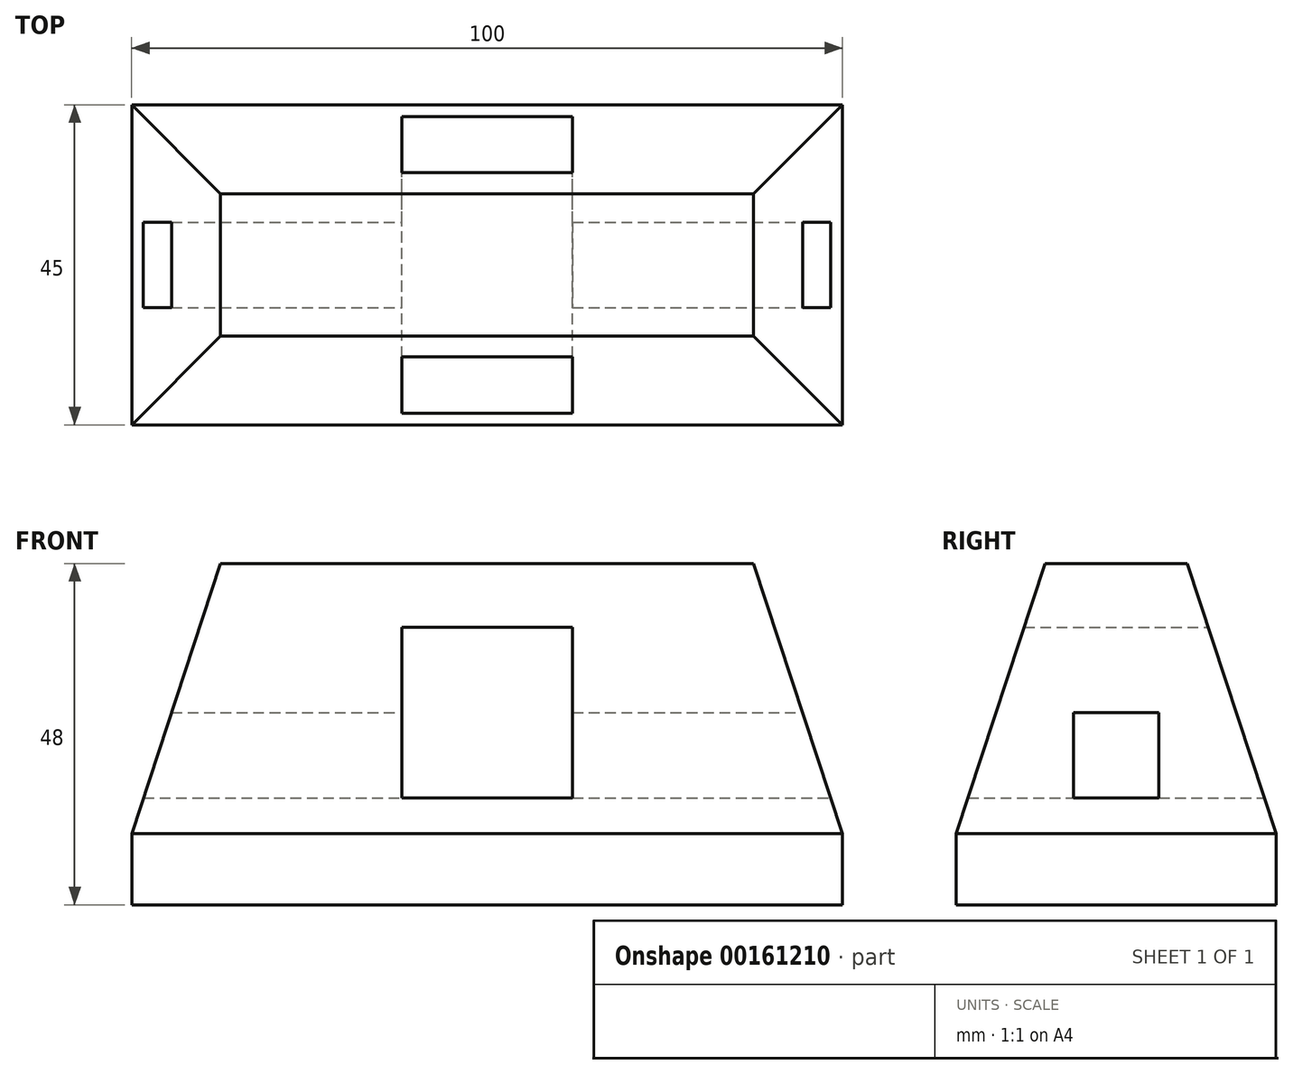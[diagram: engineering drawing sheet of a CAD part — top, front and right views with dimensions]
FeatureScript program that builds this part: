
annotation { "Feature Type Name" : "Feature", "Feature Type Description" : "" }
export const myFeature = defineFeature(function(context is Context, id is Id, definition is map)
    precondition{}
    {
        {
            var Q0;
            Q0=qCreatedBy(makeId("Top.planeOp"),FACE);
            var sketch = newSketch(context, id + "F0", { "sketchPlane" : qUnion([Q0])});
            skLineSegment(sketch, "E0.bottom", {"start": v(-62.77, 15.57) * mm, "end": v(37.23, 15.57) * mm});
            skLineSegment(sketch, "E0.top", {"start": v(-62.77, -29.43) * mm, "end": v(37.23, -29.43) * mm});
            skLineSegment(sketch, "E0.left", {"start": v(-62.77, 15.57) * mm, "end": v(-62.77, -29.43) * mm});
            skLineSegment(sketch, "E0.right", {"start": v(37.23, 15.57) * mm, "end": v(37.23, -29.43) * mm});
            skSolve(sketch);
        }
        {
            var Q0;
            Q0 = qSketchRegion(id + "F0", true);
            extrude(context, id + "F1", {"entities" : qUnion([Q0]), "depth" : 10 * mm});
        }
        {
            var Q0;
            Q0=makeQuery(id+"F1.opExtrude","SWEPT_FACE",FACE,{"disambiguationData":[OSD([sQuery(id+"F0.wireOp",EDGE,"E0.bottom")])]});
            var sketch = newSketch(context, id + "F2", { "sketchPlane" : qUnion([Q0])});
            skPoint(sketch, "E1.endSnap0", {"position": v(12.77, 10) * mm});
            skLineSegment(sketch, "E2", {"start": v(12.77, 48) * mm, "end": v(-24.73, 48) * mm});
            skLineSegment(sketch, "E3", {"start": v(12.77, 48) * mm, "end": v(50.27, 48) * mm});
            skLineSegment(sketch, "E4", {"start": v(-24.73, 48) * mm, "end": v(-37.23, 10) * mm});
            skLineSegment(sketch, "E5", {"start": v(50.27, 48) * mm, "end": v(62.77, 10) * mm});
            skLineSegment(sketch, "E6", {"start": v(12.77, 39) * mm, "end": v(24.77, 39) * mm});
            skLineSegment(sketch, "E7", {"start": v(24.77, 39) * mm, "end": v(24.77, 15) * mm});
            skLineSegment(sketch, "E8", {"start": v(24.77, 15) * mm, "end": v(12.77, 15) * mm});
            skLineSegment(sketch, "E9", {"start": v(12.77, 15) * mm, "end": v(0.77, 15) * mm});
            skLineSegment(sketch, "E10", {"start": v(0.77, 15) * mm, "end": v(0.77, 39) * mm});
            skLineSegment(sketch, "E11", {"start": v(0.77, 39) * mm, "end": v(12.77, 39) * mm});
            skLineSegment(sketch, "E12", {"start": v(12.77, 48) * mm, "end": v(12.77, 39) * mm});
            skLineSegment(sketch, "E13", {"start": v(12.77, 15) * mm, "end": v(12.77, 10) * mm});
            skSolve(sketch);
        }
        {
            var Q0;
            Q0=makeQuery(id+"F2.imprint","IMPRINT",FACE,{"disambiguationData":[TD([[makeQuery(id+"F2.imprint","IMPRINT",EDGE,{"derivedFrom":sQuery(id+"F2.wireOp",EDGE,"E2")}),1.0]])]});
            var Q1;
            Q1=makeQuery(id+"F2.imprint","IMPRINT",FACE,{"disambiguationData":[TD([[makeQuery(id+"F2.imprint","IMPRINT",EDGE,{"derivedFrom":sQuery(id+"F2.wireOp",EDGE,"E3")}),-1.0]])]});
            extrude(context, id + "F3", {"entities" : qUnion([Q0, Q1]), "operationType" : NewBodyOperationType.ADD, "oppositeDirection" : true, "depth" : 45 * mm});
        }
        {
            var Q0;
            Q0=makeQuery(id+"F1.opExtrude","SWEPT_FACE",FACE,{"disambiguationData":[OSD([sQuery(id+"F0.wireOp",EDGE,"E0.right")])]});
            var sketch = newSketch(context, id + "F4", { "sketchPlane" : qUnion([Q0])});
            skLineSegment(sketch, "E14", {"start": v(-6.93, 48) * mm, "end": v(-16.93, 48) * mm});
            skLineSegment(sketch, "E15", {"start": v(-16.93, 48) * mm, "end": v(-29.43, 10) * mm});
            skLineSegment(sketch, "E16", {"start": v(-6.93, 48) * mm, "end": v(3.07, 48) * mm});
            skLineSegment(sketch, "E17", {"start": v(3.07, 48) * mm, "end": v(15.57, 10) * mm});
            skLineSegment(sketch, "E18", {"start": v(-6.93, 27) * mm, "end": v(-0.93, 27) * mm});
            skLineSegment(sketch, "E19", {"start": v(-0.93, 27) * mm, "end": v(-0.93, 15) * mm});
            skLineSegment(sketch, "E20", {"start": v(-0.93, 15) * mm, "end": v(-12.93, 15) * mm});
            skLineSegment(sketch, "E21", {"start": v(-12.93, 15) * mm, "end": v(-12.93, 27) * mm});
            skLineSegment(sketch, "E22", {"start": v(-12.93, 27) * mm, "end": v(-6.93, 27) * mm});
            skLineSegment(sketch, "E23", {"start": v(-29.43, 10) * mm, "end": v(-29.43, 48) * mm});
            skLineSegment(sketch, "E24", {"start": v(-29.43, 48) * mm, "end": v(-16.93, 48) * mm});
            skLineSegment(sketch, "E25", {"start": v(3.07, 48) * mm, "end": v(15.57, 48) * mm});
            skLineSegment(sketch, "E26", {"start": v(15.57, 48) * mm, "end": v(15.57, 10) * mm});
            skSolve(sketch);
        }
        {
            var Q0;
            Q0 = qSketchRegion(id + "F4", true);
            extrude(context, id + "F5", {"entities" : qUnion([Q0]), "operationType" : NewBodyOperationType.REMOVE, "oppositeDirection" : true, "depth" : 122 * mm});
        }
    });
